# Revit family: Cleanroom_Pass-Through_TerraUni_Clean-Seam-Floor-mount
name_source: partatom
category: Specialty Equipment
units: mm (PartAtom-declared; Revit-internal decimal feet)

## family parameters
Classification Number = 23.40.70.11.11.11.11
Cut with Voids When Loaded = No
Enable Cutting in Views = No
Host = Face
Maintain Annotation Orientation = No
Part Type = Normal
Room Calculation Point = No
Round Connector Dimension = Use Diameter
Shared = No

## types (6) — shared parameters
Assembly Code = E1020700
Construction Details = http://www.arcat.com
Default Elevation = 4' - 0"
Include Rack System = Yes
Include ULPA Air Shower = Yes
Keynote = 13 20 00
Manufacturer = Terra Universal, Inc.
Manufacturer Fax = 714-992-2179
Manufacturer Website = http://www.terrauniversal.com
Model_Rack System = Not Applicable
Product Data = http://www.arcat.com
Revision = R1_3_2012
Sales Information = http://www.terrauniversal.com
Send Message = http://www.arcat.com Universal, Inc.&coid=43448&rep=147&fax=714-992-2179&mf=
Specification = http://www.arcat.com
URL = http://www.terrauniversal.com
zero-valued in all types: Expected Lifespan (Years), Maintenance Schedule (Months), Warranty Duration (Years)

## per-type parameters (varying)
| type | Description | Door Style | Fixture Material | Model | Opening Height | Opening Width | Overall Height | Overall Width | Unit Depth | Unit Height | Unit Width |
| 36x36x48 Regular 304 SS | Terra Universal 2636-14C CleanSeam Stainless Steel Pass-Through Chamber | NonFireRated-Door : Windowed Door 4 Handle | Metal - TerraUniversal - 304 SS | 2636-14C | 4' - 0 1/2" | 3' - 1" | 4' - 2" | 3' - 4" | 3' - 0" | 4' - 0" | 3' - 0" |
| 36x36x36 Regular 304 SS | Terra Universal 2636-13C CleanSeam Stainless Steel Pass-Through Chamber | NonFireRated-Door : Windowed Door 3 Handle | Metal - TerraUniversal - 304 SS | 2636-13C | 3' - 0 1/2" | 3' - 1" | 3' - 2" | 3' - 4" | 3' - 0" | 3' - 0" | 3' - 0" |
| 24x24x36 Regular 304 SS | Terra Universal 2636-12C CleanSeam Stainless Steel Pass-Through Chamber | NonFireRated-Door : Windowed Door 3 Handle | Metal - TerraUniversal - 304 SS | 2636-12C | 3' - 0 1/2" | 2' - 1" | 3' - 2" | 2' - 4" | 2' - 0" | 3' - 0" | 2' - 0" |
| 36x36x48 Electropolished 304 SS | Terra Universal 2636-14C-2 CleanSeam Stainless Steel Pass-Through Chamber | NonFireRated-Door : Windowed Door 4 Handle | Metal - TerraUniversal - Electropolished 304 SS | 2636-14C-2 | 4' - 0 1/2" | 3' - 1" | 4' - 2" | 3' - 4" | 3' - 0" | 4' - 0" | 3' - 0" |
| 36x36x36 Electropolished 304 SS | Terra Universal 2636-13C-2 CleanSeam Stainless Steel Pass-Through Chamber | NonFireRated-Door : Windowed Door 3 Handle | Metal - TerraUniversal - Electropolished 304 SS | 2636-13C-2 | 3' - 0 1/2" | 3' - 1" | 3' - 2" | 3' - 4" | 3' - 0" | 3' - 0" | 3' - 0" |
| 24x24x36 Electropolished 304 SS | Terra Universal 2636-12C-2 CleanSeam Stainless Steel Pass-Through Chamber | NonFireRated-Door : Windowed Door 3 Handle | Metal - TerraUniversal - Electropolished 304 SS | 2636-12C-2 | 3' - 0 1/2" | 2' - 1" | 3' - 2" | 2' - 4" | 2' - 0" | 3' - 0" | 2' - 0" |

## geometry (parser evidence)
native form markers: Blend x4, Sweep x3
no freeform markers — native parametric forms only
